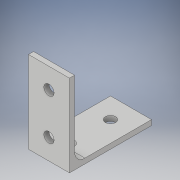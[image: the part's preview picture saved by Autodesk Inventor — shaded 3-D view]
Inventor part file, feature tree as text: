
AUTODESK INVENTOR PART (.ipt)
format: ipt  version: 2018 (Build 220112000, 112)  size: 124,416 bytes
history: native  units: in
note: dims shown in document units (in); Inventor stores cm internally (conversion verified against a paired STEP export)
features: hole x4, extrude x1, fillet x1, sketch x1
ambient origin geometry x8: Origin, YZ Plane, XZ Plane, XY Plane, X Axis, Y Axis, Z Axis, Center Point
bodies: Solid1 (feature_tree)
feature tree (7):
  extrude  "Extrusion1"  Depth=0.125in
  fillet  "Fillet1"  Radius=0.125in
  hole  "Hole1"  [1 undecoded]
  hole  "Hole2"  [1 undecoded]
  hole  "Hole3"  [1 undecoded]
  hole  "Hole4"  [1 undecoded]
  sketch  "Sketch1"  dims[d0=2.0in d1=0.125in d2=0.125in d3=2.0in d4=1.0in d5=0.0in d6=0.25in d7=0.5in d8=0.5in d9=0.25in d10=0.75in d11=0.375in d12=0.25in d13=0.5635in d14=1.0in d15=0.8108in d16=1.5in d17=0.5in d18=0.25in d19=0.75in d20=0.375in d21=0.25in d22=0.5635in d23=1.0in d24=0.8108in d25=0.5in d26=0.5in d27=0.25in d28=0.75in d29=0.375in d30=0.25in d31=0.5635in d32=1.0in d33=0.8108in d34=1.5in d35=0.5in d36=0.25in d37=0.75in d38=0.375in d39=0.25in d40=0.5635in d41=1.0in d42=0.8108in]
note: 4 required parameter values undecoded (feature->parameter linkage not recoverable at this tier; creation-order binding heuristic only, values carry confidence <= 0.55)
